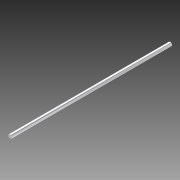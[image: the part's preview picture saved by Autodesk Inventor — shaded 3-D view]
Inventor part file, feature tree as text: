
AUTODESK INVENTOR PART (.ipt)
format: ipt  version: 2011 (Build 150239000, 239)  size: 63,488 bytes
history: native  units: in
note: dims shown in document units (in); Inventor stores cm internally (conversion verified against a paired STEP export)
features: extrude x1, sketch x1
ambient origin geometry x8: Origin, YZ Plane, XZ Plane, XY Plane, X Axis, Y Axis, Z Axis, Center Point
bodies: Solid1 (feature_tree)
feature tree (2):
  extrude  "Extrusion1"  Depth=14.0in TaperAngle=0.0deg
  sketch  "Sketch1"  dims[d0=0.325in d1=14.0in d2=0.0in]
